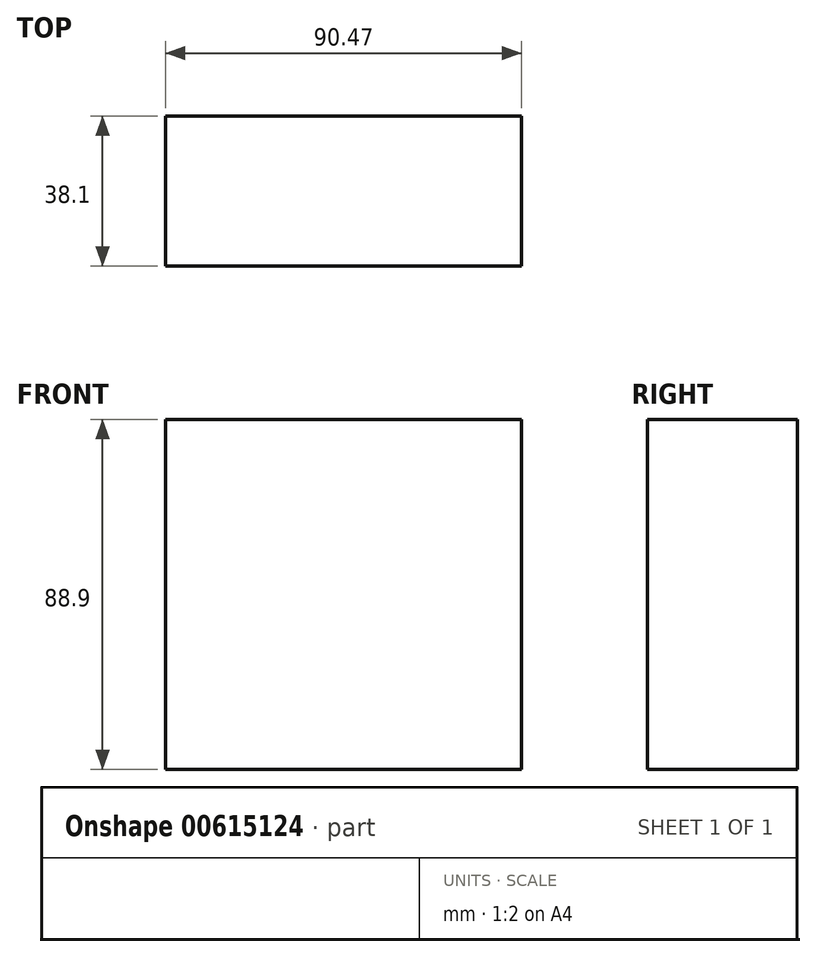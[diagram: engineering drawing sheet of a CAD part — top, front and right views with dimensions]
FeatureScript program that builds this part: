
annotation { "Feature Type Name" : "Feature", "Feature Type Description" : "" }
export const myFeature = defineFeature(function(context is Context, id is Id, definition is map)
    precondition{}
    {
        {
            var Q0;
            Q0=qCreatedBy(makeId("Right.planeOp"),FACE);
            var sketch = newSketch(context, id + "F0", { "sketchPlane" : qUnion([Q0])});
            skLineSegment(sketch, "E0.bottom", {"start": v(29.15, 407.2) * mm, "end": v(-61.33, 407.2) * mm});
            skLineSegment(sketch, "E0.top", {"start": v(29.15, -253.2) * mm, "end": v(-61.33, -253.2) * mm});
            skLineSegment(sketch, "E0.left", {"start": v(29.15, 407.2) * mm, "end": v(29.15, -253.2) * mm});
            skLineSegment(sketch, "E0.right", {"start": v(-61.33, 407.2) * mm, "end": v(-61.33, -253.2) * mm});
            skLineSegment(sketch, "E1.bottom", {"start": v(29.15, 407.2) * mm, "end": v(-8.95, 407.2) * mm});
            skLineSegment(sketch, "E1.top", {"start": v(29.15, 318.3) * mm, "end": v(-8.95, 318.3) * mm});
            skLineSegment(sketch, "E1.left", {"start": v(29.15, 407.2) * mm, "end": v(29.15, 318.3) * mm});
            skLineSegment(sketch, "E1.right", {"start": v(-8.95, 407.2) * mm, "end": v(-8.95, 318.3) * mm});
            skLineSegment(sketch, "E2.bottom", {"start": v(-24.25, -88.1) * mm, "end": v(-62.35, -88.1) * mm});
            skLineSegment(sketch, "E2.top", {"start": v(-24.25, -177) * mm, "end": v(-62.35, -177) * mm});
            skLineSegment(sketch, "E2.left", {"start": v(-24.25, -88.1) * mm, "end": v(-24.25, -177) * mm});
            skLineSegment(sketch, "E2.right", {"start": v(-62.35, -88.1) * mm, "end": v(-62.35, -177) * mm});
            skSolve(sketch);
        }
        {
            var Q0;
            {var subQ1=sQuery(id+"F0.wireOp",EDGE,"E0.bottom");Q0=makeQuery(id+"F0.imprint","IMPRINT",FACE,{"disambiguationData":[TD([[makeQuery(id+"F0.imprint","IMPRINT",EDGE,{"derivedFrom":subQ1}),1.0]])]});}
            extrude(context, id + "F1", {"entities" : qUnion([Q0]), "depth" : 90.47 * mm});
        }
    });
